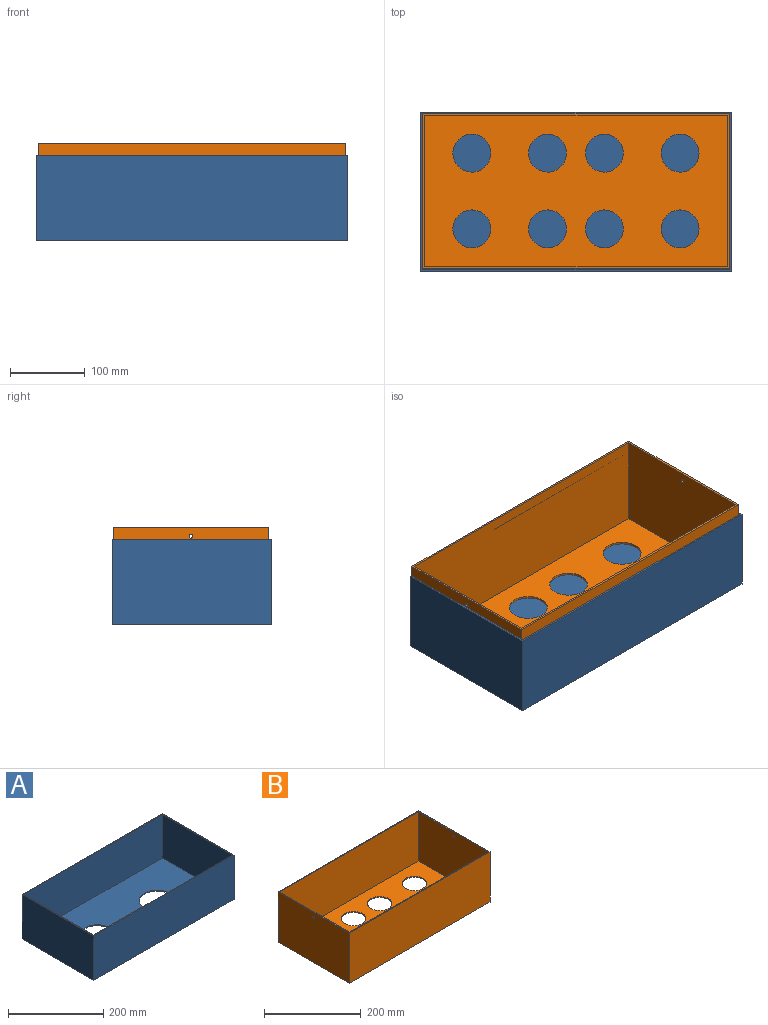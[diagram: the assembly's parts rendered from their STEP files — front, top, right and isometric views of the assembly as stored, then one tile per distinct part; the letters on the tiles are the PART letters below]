
ASSEMBLY  parts=2 mates=1
PART A: 13 faces, bbox 416.6x213.4x114.3 mm
  f0: plane 416.56x114.3mm, normal (0,-1,0), area 47612.8mm2, adj f1,f7,f8,f9
  f1: plane 213.36x114.3mm, normal (1,0,0), area 24387mm2, adj f0,f2,f8,f9
  f2: plane 416.56x114.3mm, normal (0,1,0), area 47612.8mm2, adj f1,f7,f8,f9
  f3: plane 208.28x111.76mm, normal (-1,0,0), area 23277.4mm2, adj f4,f6,f8,f10
  f4: plane 411.48x111.76mm, normal (0,1,0), area 45987mm2, adj f3,f5,f8,f10
  f5: plane 208.28x111.76mm, normal (1,0,0), area 23277.4mm2, adj f4,f6,f8,f10
  f6: plane 411.48x111.76mm, normal (0,-1,0), area 45987mm2, adj f3,f5,f8,f10
  f7: plane 213.36x114.3mm, normal (-1,0,0), area 24387mm2, adj f0,f2,f8,f9
  f8: plane 416.56x213.36mm, normal (0,0,1), area 3174.2mm2, adj f0,f1,f2,f3,f4,f5,f6,f7
  f9: plane 416.56x213.36mm, normal (0,0,-1), area 79756.5mm2, adj f0,f1,f2,f7,f11,f12
  f10: plane 411.48x208.28mm, normal (0,0,1), area 76582.3mm2, adj f3,f4,f5,f6,f11,f12
  f11: cylinder r=38.1mm len=76.2mm, axis (0,0,-1), area 608mm2, adj f9,f10
  f12: cylinder r=38.1mm len=76.2mm, axis (0,0,-1), area 608mm2, adj f9,f10
PART B: 25 faces, bbox 411.5x208.3x129.5 mm
  f0: plane 406.4x203.2mm, normal (0,0,1), area 66365.8mm2, adj f5,f6,f7,f8,f13,f14,f15,f16
  f1: plane 411.48x208.28mm, normal (0,0,-1), area 60367.7mm2, adj f2,f3,f4,f9,f13,f14,f15,f16
  f2: plane 411.48x127mm, normal (0,-1,0), area 52258mm2, adj f1,f3,f9,f10
  f3: plane 208.28x127mm, normal (1,0,0), area 26431.3mm2, adj f1,f2,f4,f10,f12
  f4: plane 411.48x127mm, normal (0,1,0), area 52258mm2, adj f1,f3,f9,f10
  f5: plane 203.2x124.46mm, normal (-1,0,0), area 25270mm2, adj f0,f6,f8,f10,f12
  f6: plane 406.4x124.46mm, normal (0,1,0), area 50580.5mm2, adj f0,f5,f7,f10
  f7: plane 203.2x124.46mm, normal (1,0,0), area 25270mm2, adj f0,f6,f8,f10,f11
  f8: plane 406.4x124.46mm, normal (0,-1,0), area 50580.5mm2, adj f0,f5,f7,f10
  f9: plane 208.28x127mm, normal (-1,0,0), area 26431.3mm2, adj f1,f2,f4,f10,f11
  f10: plane 411.48x208.28mm, normal (0,0,1), area 3122.6mm2, adj f2,f3,f4,f5,f6,f7,f8,f9
  f11: cylinder r=2.54mm len=5.08mm, axis (1,0,0), area 40.5mm2, adj f7,f9
  f12: cylinder r=2.54mm len=5.08mm, axis (1,0,0), area 40.5mm2, adj f3,f5
  f13: cylinder r=25.4mm len=50.8mm, axis (0,0,-1), area 405.4mm2, adj f0,f1
  f14: cylinder r=25.4mm len=50.8mm, axis (0,0,-1), area 405.4mm2, adj f0,f1
  f15: cylinder r=25.4mm len=50.8mm, axis (0,0,-1), area 405.4mm2, adj f0,f1
  f16: cylinder r=25.4mm len=50.8mm, axis (0,0,-1), area 405.4mm2, adj f0,f1
  f17: cylinder r=25.4mm len=50.8mm, axis (0,0,-1), area 405.4mm2, adj f0,f1
  f18: cylinder r=25.4mm len=50.8mm, axis (0,0,-1), area 405.4mm2, adj f0,f1
  f19: cylinder r=25.4mm len=50.8mm, axis (0,0,-1), area 405.4mm2, adj f0,f1
  f20: cylinder r=25.4mm len=50.8mm, axis (0,0,-1), area 405.4mm2, adj f0,f1
  f21: cylinder r=38.1mm len=76.2mm, axis (0,0,1), area 608mm2, adj f1,f22
  f22: plane 76.2x76.2mm, normal (0,0,-1), area 4560.4mm2, adj f21
  f23: cylinder r=38.1mm len=76.2mm, axis (0,0,1), area 608mm2, adj f1,f24
  f24: plane 76.2x76.2mm, normal (0,0,-1), area 4560.4mm2, adj f23
PLACE A t=(191.63,127.03,-79.69)mm
PLACE B t=(191.63,128.43,-76.92)mm
MATE slider B.f23 <-> A.f11  axis (0,0,-1) through (280.53,128.43,-79.46)mm
